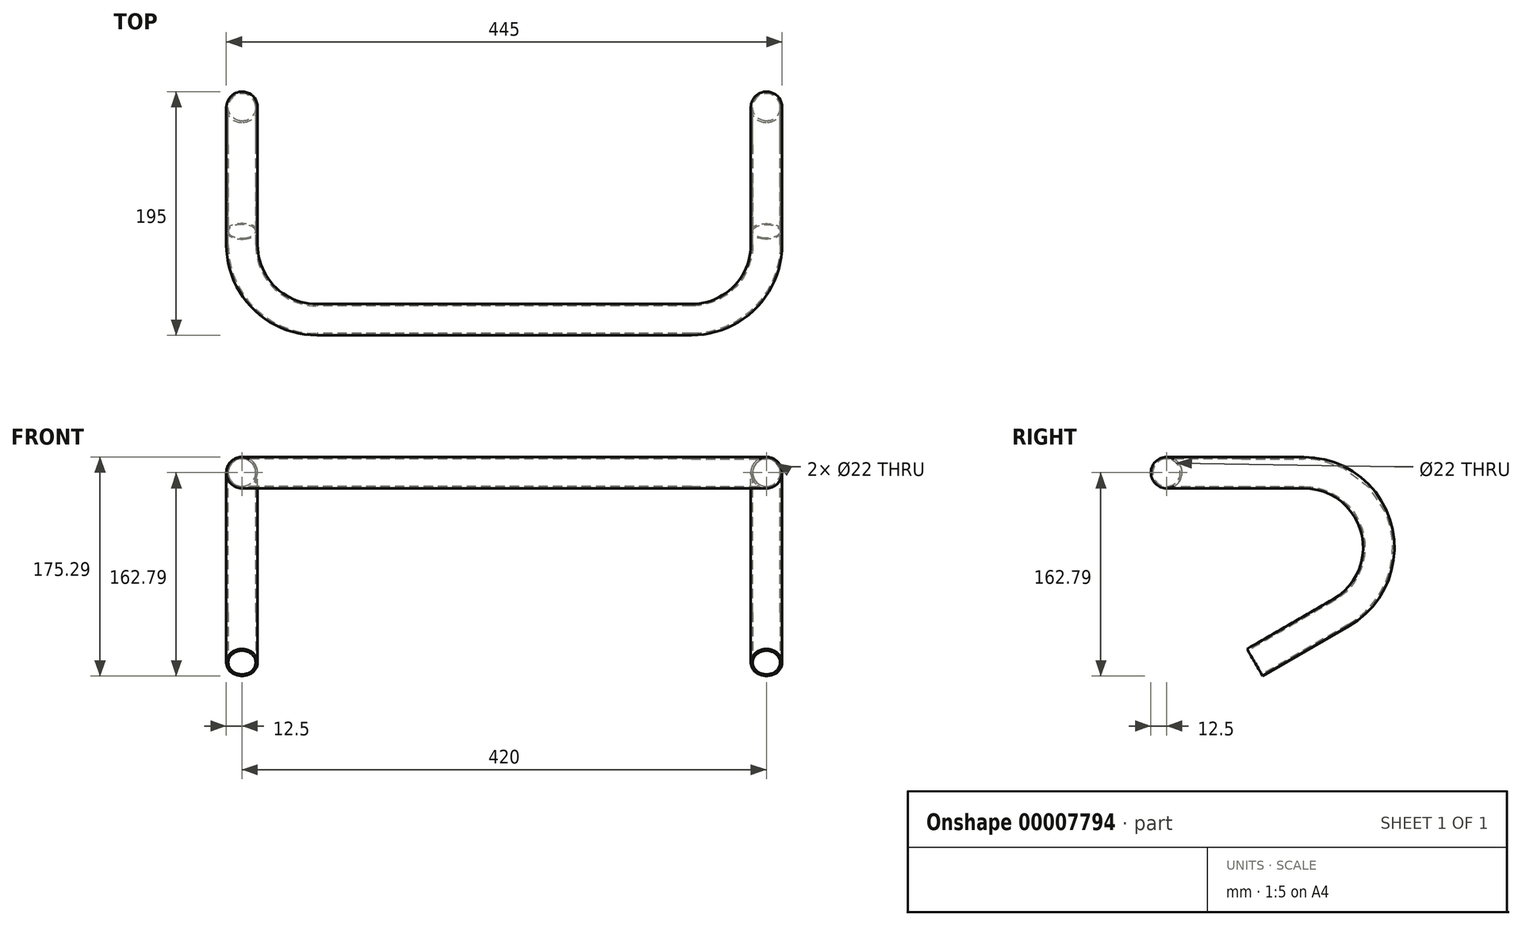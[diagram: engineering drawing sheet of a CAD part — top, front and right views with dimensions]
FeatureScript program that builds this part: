
annotation { "Feature Type Name" : "Feature", "Feature Type Description" : "" }
export const myFeature = defineFeature(function(context is Context, id is Id, definition is map)
    precondition{}
    {
        {
            var Q0;
            Q0=qCreatedBy(makeId("Right.planeOp"),FACE);
            var sketch = newSketch(context, id + "F0", { "sketchPlane" : qUnion([Q0])});
            skCircle(sketch, "E0", {"center": v(0, 0) * mm, "radius": 12.5 * mm});
            skCircle(sketch, "E1.0", {"center": v(0, 0) * mm, "radius": 11 * mm});
            skSolve(sketch);
        }
        {
            var Q0;
            Q0=qCreatedBy(makeId("Top.planeOp"),FACE);
            var sketch = newSketch(context, id + "F1", { "sketchPlane" : qUnion([Q0])});
            skLineSegment(sketch, "E2", {"start": v(-150, 0) * mm, "end": v(0, 0) * mm});
            skArc(sketch, "E3", {"start": v(150, 0) * mm, "mid": v(192.43, 17.57) * mm, "end": v(210, 60) * mm});
            skArc(sketch, "E4", {"start": v(-150, 0) * mm, "mid": v(-192.43, 17.57) * mm, "end": v(-210, 60) * mm});
            skLineSegment(sketch, "E5", {"start": v(210, 60) * mm, "end": v(210, 110) * mm});
            skLineSegment(sketch, "E6", {"start": v(-210, 60) * mm, "end": v(-210, 110) * mm});
            skLineSegment(sketch, "E7", {"start": v(150, 0) * mm, "end": v(150, 60) * mm, "construction": true});
            skLineSegment(sketch, "E8", {"start": v(210, 60) * mm, "end": v(150, 60) * mm, "construction": true});
            skLineSegment(sketch, "E9", {"start": v(-210, 60) * mm, "end": v(-150, 60) * mm, "construction": true});
            skLineSegment(sketch, "E10", {"start": v(-150, 60) * mm, "end": v(-150, 0) * mm, "construction": true});
            skLineSegment(sketch, "E11", {"start": v(0, 0) * mm, "end": v(150, 0) * mm});
            skSolve(sketch);
        }
        {
            var Q0;
            Q0=sQuery(id+"F1.wireOp",EDGE,"E5");
            cPlane(context, id + "F2", {"entities" : qUnion([Q0]), "cplaneType" : CPlaneType.LINE_ANGLE, "offset" : 150 * mm, "angle" : 90 * degree, "width" : 150 * mm, "height" : 150 * mm});
        }
        {
            var Q0;
            Q0=sQuery(id+"F1.wireOp",EDGE,"E6");
            cPlane(context, id + "F3", {"entities" : qUnion([Q0]), "cplaneType" : CPlaneType.LINE_ANGLE, "offset" : 150 * mm, "angle" : 90 * degree, "width" : 150 * mm, "height" : 150 * mm});
        }
        {
            var Q0;
            Q0=qCreatedBy(id+"F2.planeOp",FACE);
            var sketch = newSketch(context, id + "F4", { "sketchPlane" : qUnion([Q0])});
            skArc(sketch, "E12", {"start": v(140, -111.96) * mm, "mid": v(167.96, -44.47) * mm, "end": v(110, 0) * mm});
            skLineSegment(sketch, "E13", {"start": v(110, 0) * mm, "end": v(110, -60) * mm, "construction": true});
            skLineSegment(sketch, "E14", {"start": v(140, -111.96) * mm, "end": v(110, -60) * mm, "construction": true});
            skLineSegment(sketch, "E15", {"start": v(140, -111.96) * mm, "end": v(70.72, -151.96) * mm});
            skSolve(sketch);
        }
        {
            var Q0;
            Q0=qCreatedBy(id+"F3.planeOp",FACE);
            var sketch = newSketch(context, id + "F5", { "sketchPlane" : qUnion([Q0])});
            skArc(sketch, "E16", {"start": v(140, -111.96) * mm, "mid": v(167.96, -44.47) * mm, "end": v(110, 0) * mm});
            skLineSegment(sketch, "E17", {"start": v(110, 0) * mm, "end": v(110, -60) * mm, "construction": true});
            skLineSegment(sketch, "E18", {"start": v(140, -111.96) * mm, "end": v(110, -60) * mm, "construction": true});
            skLineSegment(sketch, "E19", {"start": v(140, -111.96) * mm, "end": v(70.72, -151.96) * mm});
            skSolve(sketch);
        }
        {
            var Q0;
            Q0=makeQuery(id+"F0.imprint","IMPRINT",FACE,{"disambiguationData":[TD([[makeQuery(id+"F0.imprint","IMPRINT",EDGE,{"derivedFrom":sQuery(id+"F0.wireOp",EDGE,"E0")}),1.0]])]});
            var Q1;
            Q1=sQuery(id+"F1.wireOp",EDGE,"E2");
            var Q2;
            Q2=sQuery(id+"F1.wireOp",EDGE,"E4");
            var Q3;
            Q3=sQuery(id+"F1.wireOp",EDGE,"E6");
            var Q4;
            Q4=sQuery(id+"F5.wireOp",EDGE,"E16");
            var Q5;
            Q5=sQuery(id+"F5.wireOp",EDGE,"E19");
            sweep(context, id + "F6", {"profiles" : qUnion([Q0]), "path" : qUnion([Q1, Q2, Q3, Q4, Q5])});
        }
        {
            var Q0;
            Q0=makeQuery(id+"F0.imprint","IMPRINT",FACE,{"disambiguationData":[TD([[makeQuery(id+"F0.imprint","IMPRINT",EDGE,{"derivedFrom":sQuery(id+"F0.wireOp",EDGE,"E0")}),1.0]])]});
            var Q1;
            Q1=sQuery(id+"F1.wireOp",EDGE,"E11");
            var Q2;
            Q2=sQuery(id+"F1.wireOp",EDGE,"E3");
            var Q3;
            Q3=sQuery(id+"F1.wireOp",EDGE,"E5");
            var Q4;
            Q4=sQuery(id+"F4.wireOp",EDGE,"E12");
            var Q5;
            Q5=sQuery(id+"F4.wireOp",EDGE,"E15");
            sweep(context, id + "F7", {"operationType" : NewBodyOperationType.ADD, "profiles" : qUnion([Q0]), "path" : qUnion([Q1, Q2, Q3, Q4, Q5])});
        }
    });
